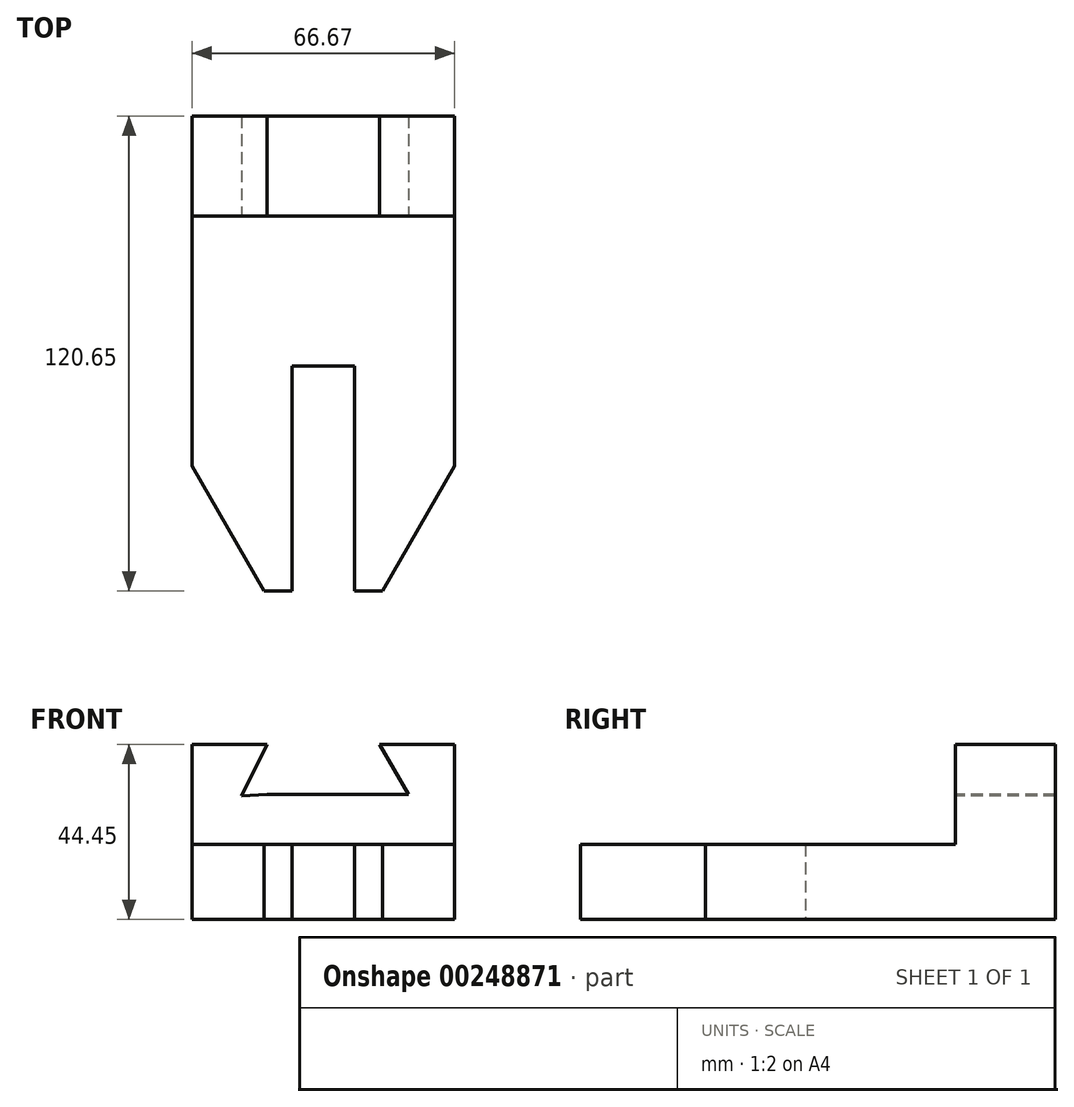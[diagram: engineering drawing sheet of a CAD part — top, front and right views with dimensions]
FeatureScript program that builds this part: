
annotation { "Feature Type Name" : "Feature", "Feature Type Description" : "" }
export const myFeature = defineFeature(function(context is Context, id is Id, definition is map)
    precondition{}
    {
        {
            var Q0;
            Q0=qCreatedBy(makeId("Top.planeOp"),FACE);
            var sketch = newSketch(context, id + "F0", { "sketchPlane" : qUnion([Q0])});
            skLineSegment(sketch, "E0", {"start": v(-39.7, 37.48) * mm, "end": v(26.97, 37.48) * mm});
            skLineSegment(sketch, "E1", {"start": v(26.97, 37.48) * mm, "end": v(26.97, -26.02) * mm});
            skLineSegment(sketch, "E2", {"start": v(26.97, -26.02) * mm, "end": v(8.64, -57.77) * mm});
            skLineSegment(sketch, "E3", {"start": v(8.64, -57.77) * mm, "end": v(1.57, -57.77) * mm});
            skLineSegment(sketch, "E4", {"start": v(1.57, -57.77) * mm, "end": v(1.57, -0.62) * mm});
            skLineSegment(sketch, "E5", {"start": v(1.57, -0.62) * mm, "end": v(-14.3, -0.62) * mm});
            skLineSegment(sketch, "E6", {"start": v(-14.3, -0.62) * mm, "end": v(-14.3, -57.77) * mm});
            skLineSegment(sketch, "E7", {"start": v(-14.3, -57.77) * mm, "end": v(-21.37, -57.77) * mm});
            skLineSegment(sketch, "E8", {"start": v(-21.37, -57.77) * mm, "end": v(-39.7, -26.02) * mm});
            skLineSegment(sketch, "E9", {"start": v(-39.7, -26.02) * mm, "end": v(-39.7, 37.48) * mm});
            skLineSegment(sketch, "E10", {"start": v(26.97, 37.48) * mm, "end": v(26.97, 62.88) * mm});
            skLineSegment(sketch, "E11", {"start": v(26.97, 62.88) * mm, "end": v(-39.7, 62.88) * mm});
            skLineSegment(sketch, "E12", {"start": v(-39.7, 62.88) * mm, "end": v(-39.7, 37.48) * mm});
            skLineSegment(sketch, "E13", {"start": v(26.97, -26.02) * mm, "end": v(26.97, -59.78) * mm});
            skLineSegment(sketch, "E14", {"start": v(-39.7, -26.02) * mm, "end": v(-39.7, -60.28) * mm});
            skLineSegment(sketch, "E15", {"start": v(-20.65, 62.88) * mm, "end": v(-20.65, 37.48) * mm});
            skLineSegment(sketch, "E16", {"start": v(7.92, 62.88) * mm, "end": v(7.92, 37.48) * mm});
            skSolve(sketch);
        }
        {
            var Q0;
            {var subQ4=sQuery(id+"F0.wireOp",EDGE,"E1");Q0=makeQuery(id+"F0.imprint","IMPRINT",FACE,{"disambiguationData":[TD([[makeQuery(id+"F0.imprint","IMPRINT",EDGE,{"derivedFrom":subQ4}),-1.0]])]});}
            extrude(context, id + "F1", {"entities" : qUnion([Q0]), "depth" : 19.05 * mm});
        }
        {
            var Q0;
            {var subQ0=sQuery(id+"F0.wireOp",EDGE,"E15");Q0=makeQuery(id+"F0.imprint","IMPRINT",FACE,{"disambiguationData":[TD([[makeQuery(id+"F0.imprint","IMPRINT",EDGE,{"derivedFrom":subQ0}),1.0]])]});}
            extrude(context, id + "F2", {"entities" : qUnion([Q0]), "operationType" : NewBodyOperationType.ADD, "depth" : 31.75 * mm});
        }
        {
            var Q0;
            {var subQ0=sQuery(id+"F0.wireOp",EDGE,"E12");Q0=makeQuery(id+"F0.imprint","IMPRINT",FACE,{"disambiguationData":[TD([[makeQuery(id+"F0.imprint","IMPRINT",EDGE,{"derivedFrom":subQ0}),1.0]])]});}
            var Q1;
            {var subQ0=sQuery(id+"F0.wireOp",EDGE,"E10");Q1=makeQuery(id+"F0.imprint","IMPRINT",FACE,{"disambiguationData":[TD([[makeQuery(id+"F0.imprint","IMPRINT",EDGE,{"derivedFrom":subQ0}),1.0]])]});}
            extrude(context, id + "F3", {"entities" : qUnion([Q0, Q1]), "operationType" : NewBodyOperationType.ADD, "depth" : 44.45 * mm});
        }
        {
            var Q0;
            {var subQ0=sQuery(id+"F0.wireOp",EDGE,"E0");Q0=makeQuery(id+"F3.boolean.opBoolean","MERGE",FACE,{"derivedFrom":[makeQuery(id+"F2.opExtrude","SWEPT_FACE",FACE,{"disambiguationData":[OSD([subQ0])]}),makeQuery(id+"F3.opExtrude","SWEPT_FACE",FACE,{"disambiguationData":[OSD([subQ0]),TDD([makeQuery(id+"F0.imprint","IMPRINT",EDGE,{"disambiguationData":[TD([[makeQuery(id+"F0.imprint","INTERSECT",VERTEX,{"derivedFrom":[subQ0,sQuery(id+"F0.wireOp",EDGE,"E15")]}),1.0]])],"derivedFrom":subQ0})])]}),makeQuery(id+"F3.opExtrude","SWEPT_FACE",FACE,{"disambiguationData":[OSD([subQ0]),TDD([makeQuery(id+"F0.imprint","IMPRINT",EDGE,{"disambiguationData":[TD([[makeQuery(id+"F0.imprint","INTERSECT",VERTEX,{"derivedFrom":[subQ0,sQuery(id+"F0.wireOp",EDGE,"E16")]}),-1.0]])],"derivedFrom":subQ0})])]})]});}
            var sketch = newSketch(context, id + "F4", { "sketchPlane" : qUnion([Q0])});
            skLineSegment(sketch, "E17", {"start": v(-20.65, 44.45) * mm, "end": v(-27.17, 31.34) * mm});
            skLineSegment(sketch, "E18", {"start": v(-27.17, 31.34) * mm, "end": v(-20.65, 31.75) * mm});
            skLineSegment(sketch, "E19", {"start": v(7.92, 44.45) * mm, "end": v(15.25, 31.75) * mm});
            skPoint(sketch, "E19.endSnap0", {"position": v(-6.37, 31.75) * mm});
            skLineSegment(sketch, "E20", {"start": v(15.25, 31.75) * mm, "end": v(7.92, 31.75) * mm});
            skSolve(sketch);
        }
        {
            var Q0;
            Q0=makeQuery(id+"F4.imprint","IMPRINT",FACE,{"disambiguationData":[TD([[makeQuery(id+"F4.imprint","IMPRINT",EDGE,{"derivedFrom":sQuery(id+"F4.wireOp",EDGE,"E17")}),1.0]])]});
            var Q1;
            Q1=makeQuery(id+"F4.imprint","IMPRINT",FACE,{"disambiguationData":[TD([[makeQuery(id+"F4.imprint","IMPRINT",EDGE,{"derivedFrom":sQuery(id+"F4.wireOp",EDGE,"E19")}),-1.0]])]});
            extrude(context, id + "F5", {"entities" : qUnion([Q0, Q1]), "operationType" : NewBodyOperationType.REMOVE, "endBound" : BoundingType.THROUGH_ALL, "oppositeDirection" : true, "depth" : 25.4 * mm});
        }
    });
